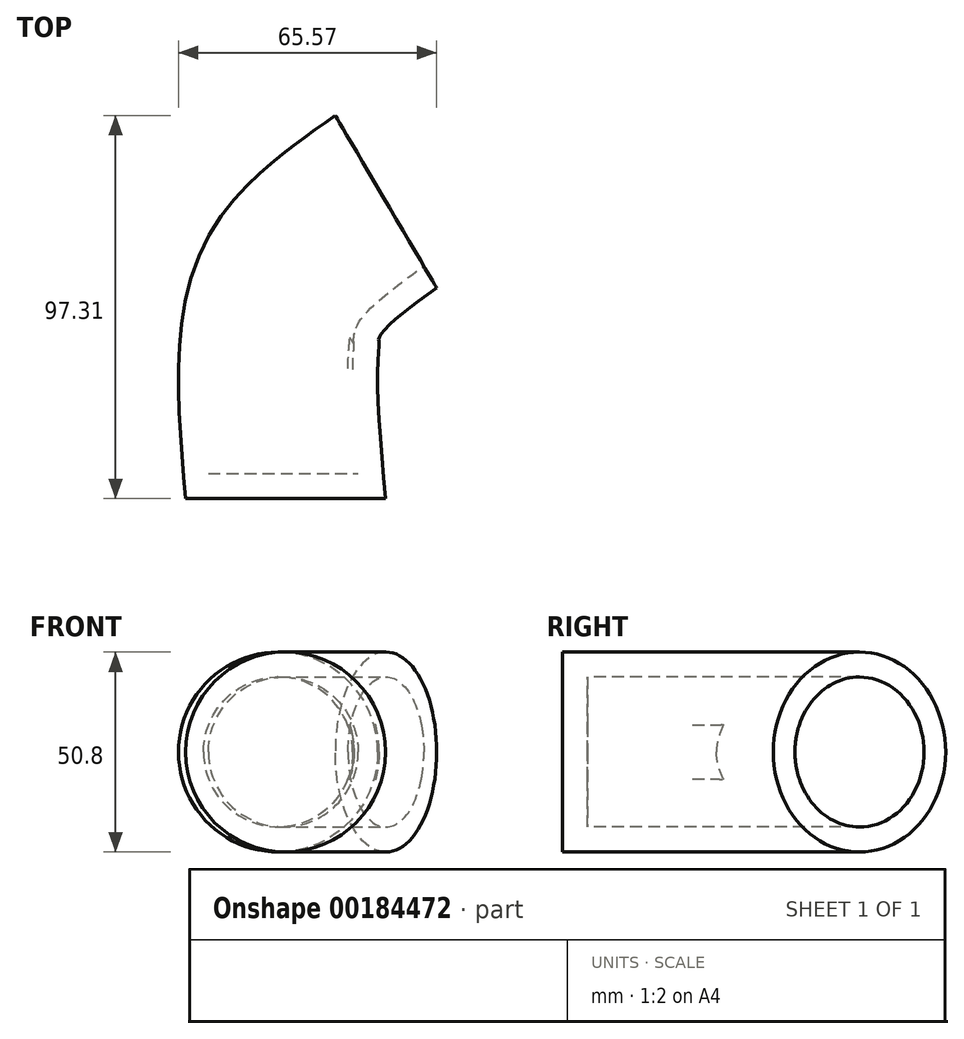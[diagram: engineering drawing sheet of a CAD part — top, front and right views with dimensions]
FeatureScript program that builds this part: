
annotation { "Feature Type Name" : "Feature", "Feature Type Description" : "" }
export const myFeature = defineFeature(function(context is Context, id is Id, definition is map)
    precondition{}
    {
        {
            var Q0;
            Q0=qCreatedBy(makeId("Front.planeOp"),FACE);
            var sketch = newSketch(context, id + "F0", { "sketchPlane" : qUnion([Q0])});
            skArc(sketch, "E0", {"start": v(25.4, 0) * mm, "mid": v(0, 25.4) * mm, "end": v(-25.4, 0) * mm});
            skPoint(sketch, "E1.start.orphan", {"position": v(-25.4, 0) * mm});
            skLineSegment(sketch, "E2", {"start": v(25.4, 0) * mm, "end": v(-25.4, 0) * mm});
            skSolve(sketch);
        }
        {
            var Q0;
            Q0=qCreatedBy(makeId("Top.planeOp"),FACE);
            var sketch = newSketch(context, id + "F1", { "sketchPlane" : qUnion([Q0])});
            skFitSpline(sketch, "E3", {"points": [v(0, 0) * mm, v(0, 47.86) * mm, v(10.58, 63.88) * mm, v(25.53, 75.42) * mm], "startDerivative": vector(-10.85, 123.38) * mm, "endDerivative": vector(56.13, 40.02) * mm});
            skSolve(sketch);
        }
        {
            var Q0;
            Q0=makeQuery(id+"F0.imprint","IMPRINT",FACE,{"disambiguationData":[TD([[makeQuery(id+"F0.imprint","IMPRINT",EDGE,{"derivedFrom":sQuery(id+"F0.wireOp",EDGE,"E0")}),1.0]])]});
            var Q1;
            Q1=sQuery(id+"F1.wireOp",EDGE,"E3");
            sweep(context, id + "F2", {"profiles" : qUnion([Q0]), "path" : qUnion([Q1])});
        }
        {
            var Q0;
            Q0=makeQuery(id+"F2.opSweep","SWEPT_BODY",BODY,{"disambiguationData":[OSD([sQuery(id+"F0.wireOp",EDGE,"E0"),sQuery(id+"F0.wireOp",EDGE,"E2"),sQuery(id+"F1.wireOp",EDGE,"E3")])]});
            var Q1;
            Q1=makeQuery(id+"F2.opSweep","SWEPT_FACE",FACE,{"disambiguationData":[OSD([sQuery(id+"F0.wireOp",EDGE,"E2"),sQuery(id+"F1.wireOp",EDGE,"E3")])]});
            mirror(context, id + "F3", {"operationType" : NewBodyOperationType.ADD, "entities" : qUnion([Q0]), "mirrorPlane" : qUnion([Q1])});
        }
        {
            var Q0;
            {var subQ0=makeQuery(id+"F2.opSweep","CAP_FACE",FACE,{"disambiguationData":[OSD([sQuery(id+"F0.wireOp",EDGE,"E0"),sQuery(id+"F0.wireOp",EDGE,"E2"),sQuery(id+"F1.wireOp",VERTEX,"E3.end")])],"isStart":false});Q0=makeQuery(id+"F3.boolean.opBoolean","MERGE",FACE,{"derivedFrom":[subQ0,makeQuery(id+"F3.opPattern","COPY",FACE,{"derivedFrom":subQ0,"instanceName":"1"})]});}
            var Q1;
            Q1=makeQuery(id+"F2.opSweep","SWEPT_BODY",BODY,{"disambiguationData":[OSD([sQuery(id+"F0.wireOp",EDGE,"E0"),sQuery(id+"F0.wireOp",EDGE,"E2"),sQuery(id+"F1.wireOp",EDGE,"E3")])]});
            shell(context, id + "F4", {"entities" : qUnion([Q0]), "parts" : qUnion([Q1]), "thickness" : 6.35 * mm});
        }
    });
